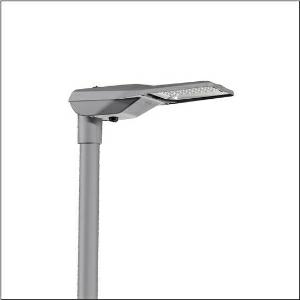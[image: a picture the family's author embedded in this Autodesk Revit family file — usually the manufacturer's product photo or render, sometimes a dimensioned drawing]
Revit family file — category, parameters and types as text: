
# Revit family: streetlight_sl_21_mini___stw1_0a_5xe2e33t08jb_e144
name_source: partatom
category: Lighting Fixtures
units: mm (PartAtom-declared; Revit-internal decimal feet)

## family parameters
Cut with Voids When Loaded = No
Host = Face
Light Source = No
Part Type = Normal
Room Calculation Point = No
Round Connector Dimension = Use Diameter
Shared = No

## types (1)
- --- (1 x LED, 12940 lm, 88.6 W, 3000K)
    Apparent Load = 89 VA
    CIE Flux Codes = 39 75 98 100 100
    Color Rendering = 70
    Color Temperature = 3000K
    Default Elevation = 1800 mm
    Description = Streetlight SL 21 mini, mast luminaire, primary light control with lens, of PMMA, primary optical cover: cover, of toughened safety glass, transparent, light distribution: STW1.0a, light emission: direct distribution, primary light characteristic: asymmetric, installation type: side-entry, post-top, LED, High Power LED, rated luminous flux: 12.940lm, luminous efficacy: 146lm/W, light colour: 730, colour temperature: 3000K, control gear: D4i, control: overheat protection, constant luminous flux control, time-dependent luminous flux control, flexible luminous flux parameterisation, pre-setting: logarithmic dimming characteristic, mains connection: 220..240V, AC, 50/60Hz, start of lifetime: 89W, end of service life: 92W, reduction: 41W, luminaire housing, of diecast aluminium, powder-coated, SITECO metallic grey (DB 702S), corrosivity category C5 high according to DIN EN ISO 12944, please order mast flange separately, inclination adjustable: 0°, 5°, 10°, 15°, sealing non-destructively replaceable, multi-level sealing system, length: 628mm, width: 235mm, height: 110mm, mast flange for spigot size: 42mm (side-entry): 5XC10008XM4, 60/48mm (side-entry/post-top): 5XC10108XM2, 76/60mm (side-entry/post-top): 5XC10108XM1, mounting height: 4..8m, Smart Interface below and above, protection rating (complete): IP66, insulation class (complete): insulation class II (safety insulation), certification: CE, ENEC, ENEC+, VDE, impact resistance: IK10, permissible operating ambient temperature for outdoor applications: -40..+50°C, standard-compliant lighting for roads and squares, packaging unit: 1 piece

Light Distribution: STW1.0a
    Height = 110 mm
    Lamp = 1 x LED
    Lamp Light Flux = 12940 lm
    Lamp Power = 88.6 W
    Lamp count = 1
    Length = 625 mm
    Luminous efficacy = 146 lm/W
    Manufacturer = Siteco
    ModVariant = No
    Model = 5XE2E33T08JB
    Number of Poles = 1
    OnlyDefault = Yes
    Power Factor = 1
    Product Name = Streetlight SL 21 mini | STW1.0a
    Product group = mast luminaire | pylon top
    ProductGroupID = 6100
    Protection Class = Protection class II
    Protection Degree = IP 66
    RLX_Detail_Level = 1
    RLX_Emergency_Light_Flux = 0 lm
    RLX_Emergency_Type = 0
    RLX_Emergency_Type_DB = No
    RlxData = <blob elided: 26445 chars, md5=68af6948>
    Socket = socket
    Standby Power = 0 W
    System Light Flux = 12940 lm
    System Power = 89 W
    Type Comments = factory setting: luminous flux: 100 % | dim-lin: 254 | 915 mA
    Type Image = l_1003514.jpg
    URL = http://relux.com
    VarID = @adj_031083
    Voltage = 0 V
    Weight = 0.00 kg
    Width = 234 mm

## geometry (parser evidence)
native form markers: Blend x4, Sweep x11
no freeform markers — native parametric forms only
